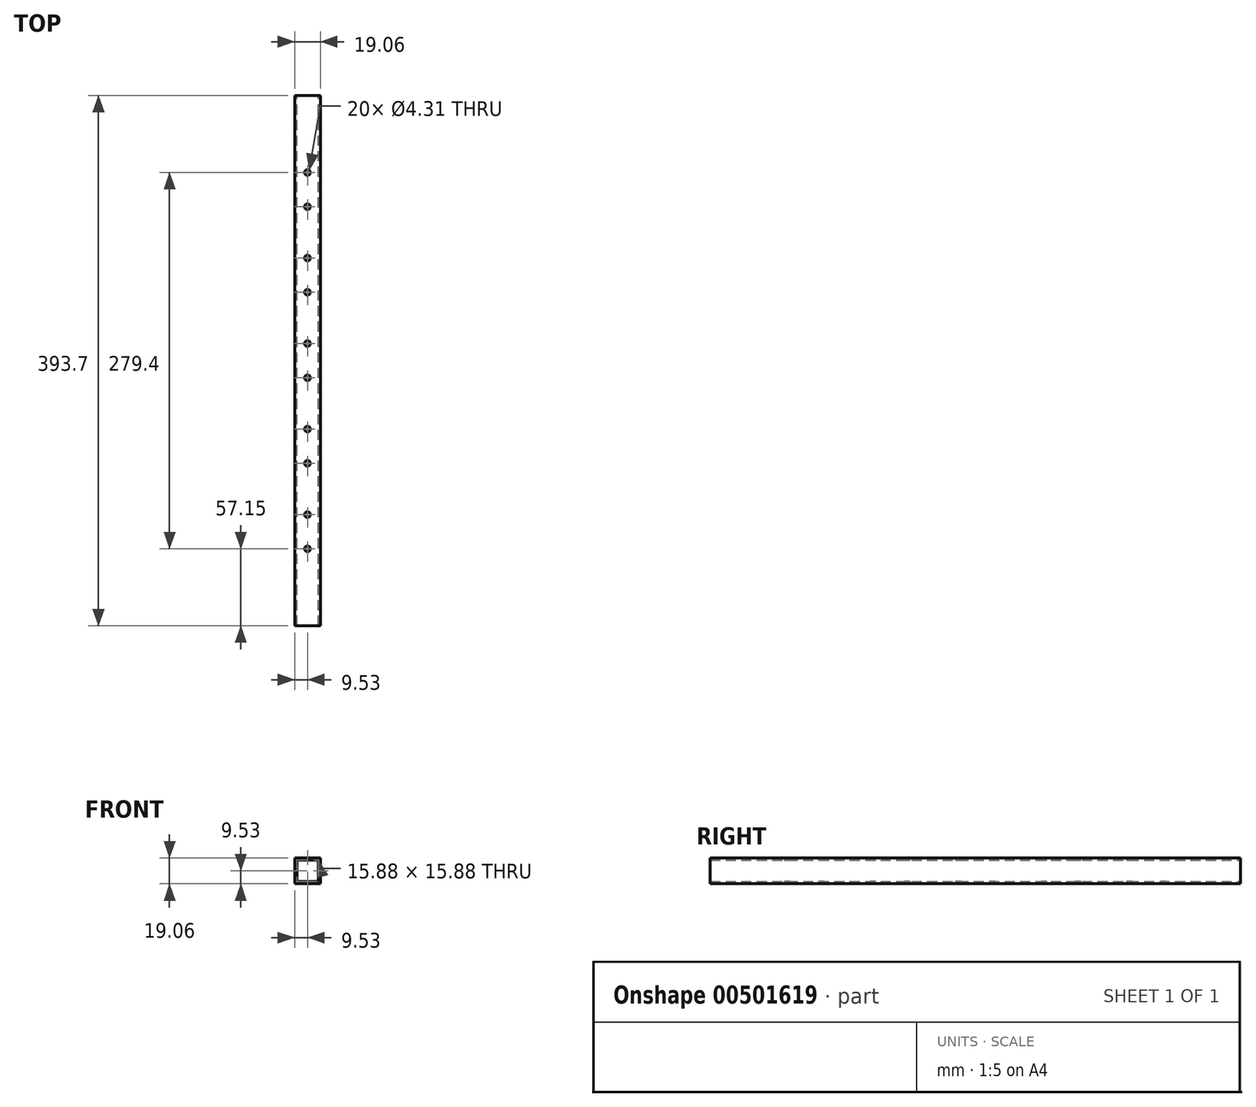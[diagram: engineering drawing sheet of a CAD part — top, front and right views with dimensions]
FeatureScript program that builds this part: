
annotation { "Feature Type Name" : "Feature", "Feature Type Description" : "" }
export const myFeature = defineFeature(function(context is Context, id is Id, definition is map)
    precondition{}
    {
        {
            var Q0;
            Q0=qCreatedBy(makeId("Front.planeOp"),FACE);
            var sketch = newSketch(context, id + "F0", { "sketchPlane" : qUnion([Q0])});
            skLineSegment(sketch, "E0.bottom", {"start": v(-9.52, 9.53) * mm, "end": v(9.53, 9.53) * mm});
            skLineSegment(sketch, "E0.top", {"start": v(-9.53, -9.53) * mm, "end": v(9.52, -9.53) * mm});
            skLineSegment(sketch, "E0.left", {"start": v(-9.52, 9.53) * mm, "end": v(-9.53, -9.52) * mm});
            skLineSegment(sketch, "E0.right", {"start": v(9.53, 9.53) * mm, "end": v(9.52, -9.52) * mm});
            skPoint(sketch, "E0.middle", {"position": v(0, 0) * mm});
            skLineSegment(sketch, "E1.bottom", {"start": v(-7.94, 7.94) * mm, "end": v(7.94, 7.94) * mm});
            skLineSegment(sketch, "E1.top", {"start": v(-7.94, -7.94) * mm, "end": v(7.94, -7.94) * mm});
            skLineSegment(sketch, "E1.left", {"start": v(-7.94, 7.94) * mm, "end": v(-7.94, -7.94) * mm});
            skLineSegment(sketch, "E1.right", {"start": v(7.94, 7.94) * mm, "end": v(7.94, -7.94) * mm});
            skSolve(sketch);
        }
        {
            var Q0;
            Q0=qSketchRegion(id+"F0",true);
            extrude(context, id + "F1", {"entities" : qUnion([Q0]), "endBound" : BoundingType.SYMMETRIC, "depth" : 393.7 * mm});
        }
        {
            var Q0;
            Q0=makeQuery(id+"F1.opExtrude","SWEPT_FACE",FACE,{"disambiguationData":[OSD([sQuery(id+"F0.wireOp",EDGE,"E0.bottom")])]});
            var sketch = newSketch(context, id + "F2", { "sketchPlane" : qUnion([Q0])});
            skCircle(sketch, "E2", {"center": v(0, 12.7) * mm, "radius": 2.15 * mm});
            skCircle(sketch, "E3.MirrorC", {"center": v(0, -12.7) * mm, "radius": 2.15 * mm});
            skCircle(sketch, "E4.0.1.0", {"center": v(0, 76.2) * mm, "radius": 2.15 * mm});
            skCircle(sketch, "E4.0.1.1", {"center": v(0, 50.8) * mm, "radius": 2.15 * mm});
            skCircle(sketch, "E4.0.2.0", {"center": v(0, 139.7) * mm, "radius": 2.15 * mm});
            skCircle(sketch, "E4.0.2.1", {"center": v(0, 114.3) * mm, "radius": 2.15 * mm});
            skLineSegment(sketch, "E4.direction1", {"start": v(0, 12.7) * mm, "end": v(25.4, 12.7) * mm, "construction": true});
            skLineSegment(sketch, "E4.direction2", {"start": v(0, 12.7) * mm, "end": v(0, 76.2) * mm, "construction": true});
            skCircle(sketch, "E5.MirrorC", {"center": v(0, -50.8) * mm, "radius": 2.15 * mm});
            skCircle(sketch, "E6.MirrorC", {"center": v(0, -76.2) * mm, "radius": 2.15 * mm});
            skCircle(sketch, "E7.MirrorC", {"center": v(0, -114.3) * mm, "radius": 2.15 * mm});
            skCircle(sketch, "E8.MirrorC", {"center": v(0, -139.7) * mm, "radius": 2.15 * mm});
            skSolve(sketch);
        }
        {
            var Q0;
            Q0=qSketchRegion(id+"F2",true);
            var Q1;
            Q1=makeQuery(id+"F1.opExtrude","SWEPT_FACE",FACE,{"disambiguationData":[OSD([sQuery(id+"F0.wireOp",EDGE,"E0.top")])]});
            extrude(context, id + "F3", {"entities" : qUnion([Q0, Q1]), "operationType" : NewBodyOperationType.REMOVE, "oppositeDirection" : true, "depth" : 25.4 * mm});
        }
    });
